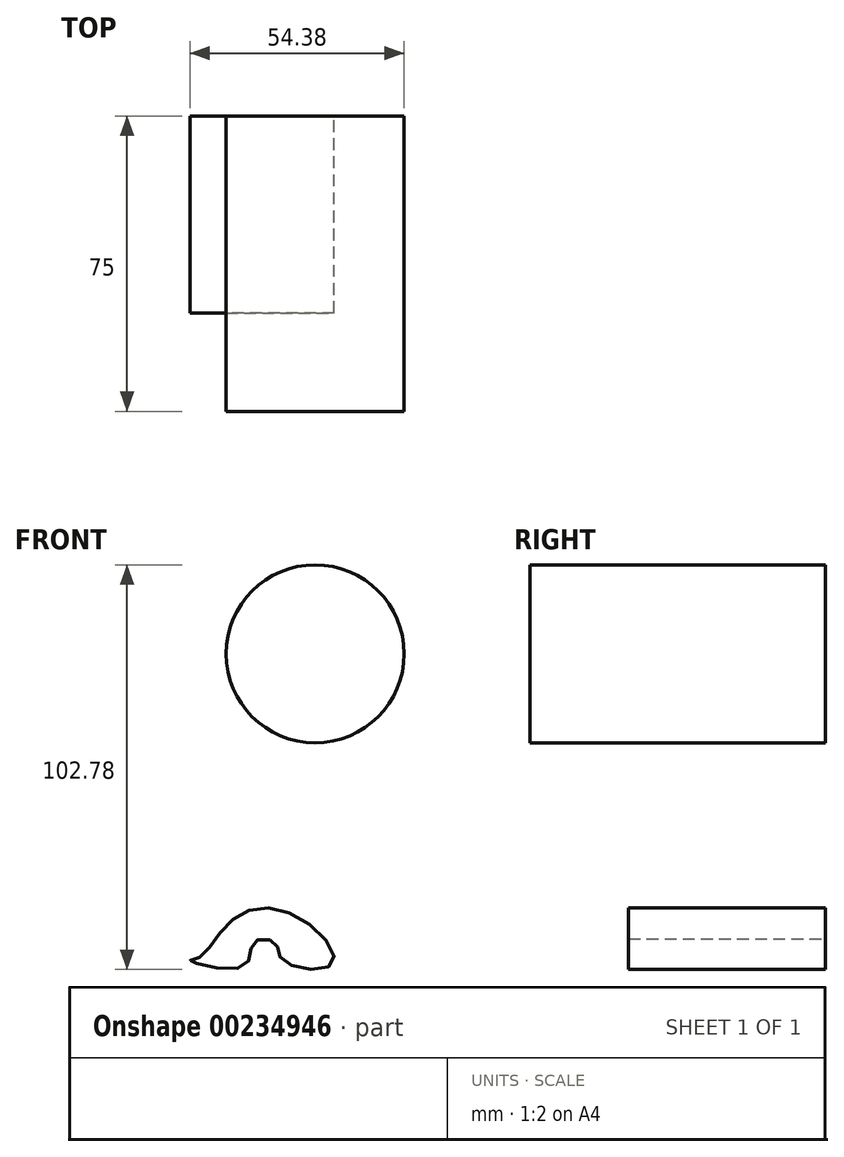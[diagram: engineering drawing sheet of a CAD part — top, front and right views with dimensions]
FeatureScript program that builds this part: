
annotation { "Feature Type Name" : "Feature", "Feature Type Description" : "" }
export const myFeature = defineFeature(function(context is Context, id is Id, definition is map)
    precondition{}
    {
        {
            var Q0;
            Q0=qCreatedBy(makeId("Front.planeOp"),FACE);
            var sketch = newSketch(context, id + "F0", { "sketchPlane" : qUnion([Q0])});
            skCircle(sketch, "E0", {"center": v(-34.22, 36.06) * mm, "radius": 22.6 * mm});
            skSolve(sketch);
        }
        {
            var Q0;
            Q0=makeQuery(id+"F0.imprint","IMPRINT",FACE,{"disambiguationData":[TD([[makeQuery(id+"F0.imprint","IMPRINT",EDGE,{"derivedFrom":sQuery(id+"F0.wireOp",EDGE,"E0")}),1.0]])]});
            extrude(context, id + "F1", {"entities" : qUnion([Q0]), "depth" : 25 * mm, "hasSecondDirection" : true, "secondDirectionOppositeDirection" : true, "secondDirectionDepth" : 25 * mm});
        }
        {
            var Q0;
            Q0=makeQuery(id+"F1.opExtrude","CAP_FACE",FACE,{"disambiguationData":[OSD([sQuery(id+"F0.wireOp",EDGE,"E0")])],"isStart":false});
            extrude(context, id + "F2", {"entities" : qUnion([Q0]), "operationType" : NewBodyOperationType.ADD, "depth" : 25 * mm, "hasSecondDirection" : true, "secondDirectionOppositeDirection" : true, "secondDirectionDepth" : 10 * mm});
        }
        {
            var Q0;
            Q0=qCreatedBy(makeId("Front.planeOp"),FACE);
            var sketch = newSketch(context, id + "F3", { "sketchPlane" : qUnion([Q0])});
            skFitSpline(sketch, "E1", {"points": [v(-63.63, -41.06) * mm, v(-55.06, -31.34) * mm, v(-38.85, -30.64) * mm, v(-29.82, -42.68) * mm, v(-42.32, -41.99) * mm, v(-44.4, -37.36) * mm, v(-49.97, -37.36) * mm, v(-52.28, -43.38) * mm, v(-65.95, -41.99) * mm, v(-63.63, -41.06) * mm]});
            skSolve(sketch);
        }
        {
            var Q0;
            Q0=makeQuery(id+"F3.imprint","IMPRINT",FACE,{"disambiguationData":[TD([[makeQuery(id+"F3.imprint","IMPRINT",EDGE,{"derivedFrom":sQuery(id+"F3.wireOp",EDGE,"E1")}),-1.0]])]});
            extrude(context, id + "F4", {"entities" : qUnion([Q0]), "depth" : 25 * mm, "hasSecondDirection" : true, "secondDirectionOppositeDirection" : true, "secondDirectionDepth" : 25 * mm});
        }
    });
